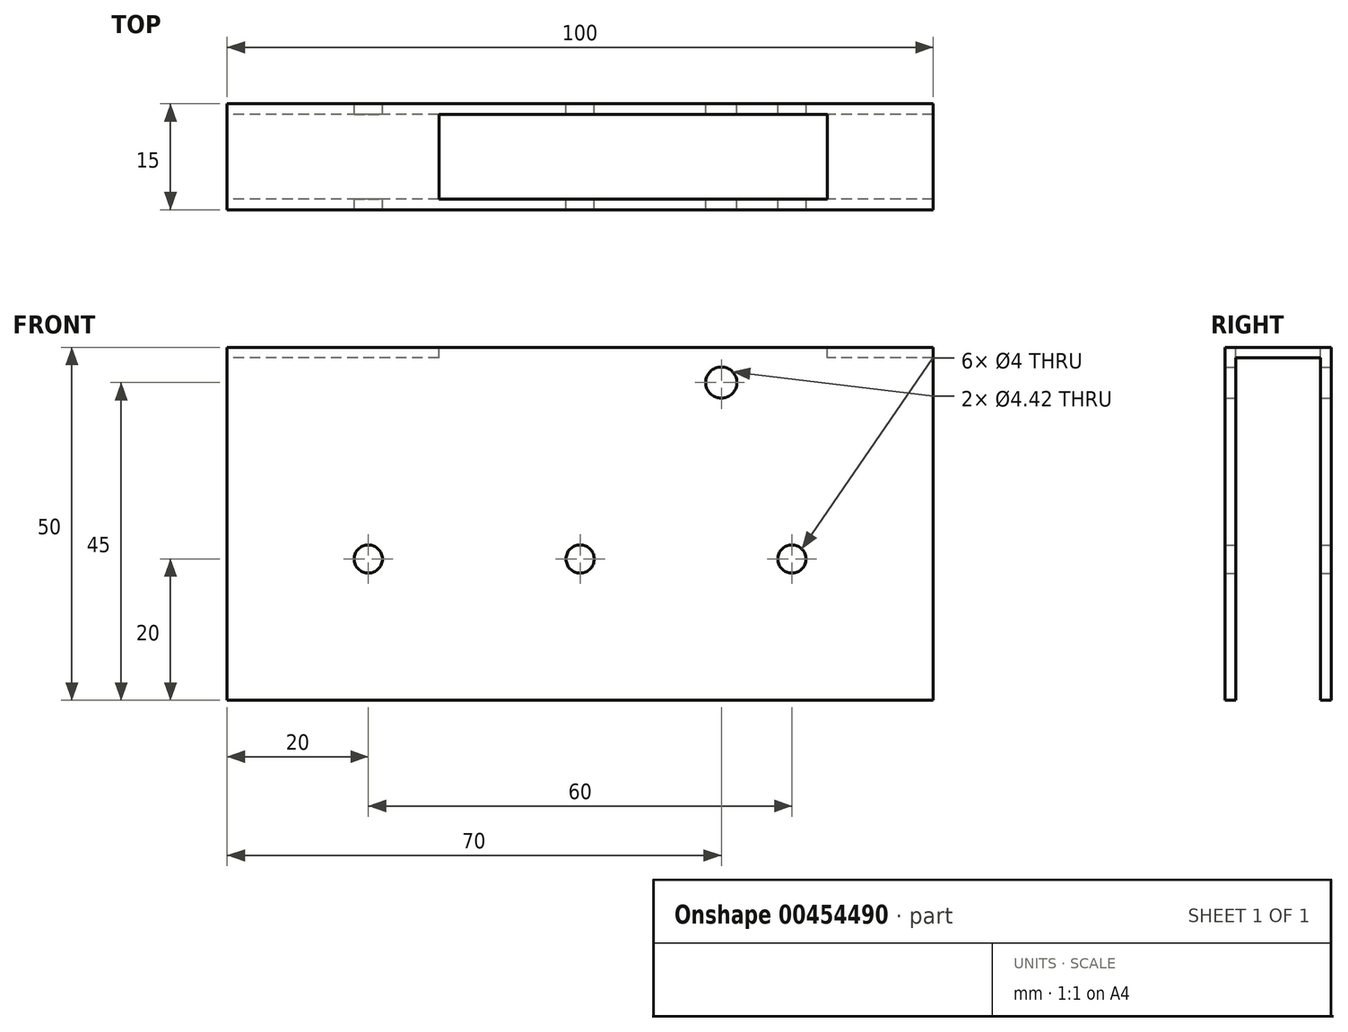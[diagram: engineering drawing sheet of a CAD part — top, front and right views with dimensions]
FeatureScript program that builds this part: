
annotation { "Feature Type Name" : "Feature", "Feature Type Description" : "" }
export const myFeature = defineFeature(function(context is Context, id is Id, definition is map)
    precondition{}
    {
        {
            var Q0;
            Q0=qCreatedBy(makeId("Front.planeOp"),FACE);
            var sketch = newSketch(context, id + "F0", { "sketchPlane" : qUnion([Q0])});
            skLineSegment(sketch, "E0.bottom", {"start": v(-50, 30) * mm, "end": v(50, 30) * mm});
            skLineSegment(sketch, "E0.top", {"start": v(-50, -20) * mm, "end": v(50, -20) * mm});
            skLineSegment(sketch, "E0.left", {"start": v(-50, 30) * mm, "end": v(-50, -20) * mm});
            skLineSegment(sketch, "E0.right", {"start": v(50, 30) * mm, "end": v(50, -20) * mm});
            skCircle(sketch, "E1", {"center": v(0, 0) * mm, "radius": 2 * mm});
            skCircle(sketch, "E2", {"center": v(-30, 0) * mm, "radius": 2 * mm});
            skCircle(sketch, "E3", {"center": v(30, 0) * mm, "radius": 2 * mm});
            skCircle(sketch, "E4", {"center": v(20, 25) * mm, "radius": 2.21 * mm});
            skSolve(sketch);
        }
        {
            var Q0;
            Q0=makeQuery(id+"F0.imprint","IMPRINT",FACE,{"disambiguationData":[TD([[makeQuery(id+"F0.imprint","IMPRINT",EDGE,{"derivedFrom":sQuery(id+"F0.wireOp",EDGE,"E0.bottom")}),-1.0]])]});
            extrude(context, id + "F1", {"entities" : qUnion([Q0]), "depth" : 15 * mm});
        }
        {
            var Q0;
            Q0=makeQuery(id+"F1.opExtrude","SWEPT_FACE",FACE,{"disambiguationData":[OSD([sQuery(id+"F0.wireOp",EDGE,"E0.left")])]});
            var sketch = newSketch(context, id + "F2", { "sketchPlane" : qUnion([Q0])});
            skLineSegment(sketch, "E5.bottom", {"start": v(1.5, -20) * mm, "end": v(13.5, -20) * mm});
            skLineSegment(sketch, "E5.top", {"start": v(1.5, 28.5) * mm, "end": v(13.5, 28.5) * mm});
            skLineSegment(sketch, "E5.left", {"start": v(1.5, -20) * mm, "end": v(1.5, 28.5) * mm});
            skLineSegment(sketch, "E5.right", {"start": v(13.5, -20) * mm, "end": v(13.5, 28.5) * mm});
            skSolve(sketch);
        }
        {
            var Q0;
            Q0 = qSketchRegion(id + "F2", true);
            extrude(context, id + "F3", {"entities" : qUnion([Q0]), "operationType" : NewBodyOperationType.REMOVE, "endBound" : BoundingType.THROUGH_ALL, "oppositeDirection" : true, "depth" : 25 * mm});
        }
        {
            var Q0;
            Q0=makeQuery(id+"F1.opExtrude","SWEPT_FACE",FACE,{"disambiguationData":[OSD([sQuery(id+"F0.wireOp",EDGE,"E0.bottom")])]});
            var sketch = newSketch(context, id + "F4", { "sketchPlane" : qUnion([Q0])});
            skLineSegment(sketch, "E6.bottom", {"start": v(35, -13.5) * mm, "end": v(-20, -13.5) * mm});
            skLineSegment(sketch, "E6.top", {"start": v(35, -1.5) * mm, "end": v(-20, -1.5) * mm});
            skLineSegment(sketch, "E6.left", {"start": v(35, -13.5) * mm, "end": v(35, -1.5) * mm});
            skLineSegment(sketch, "E6.right", {"start": v(-20, -13.5) * mm, "end": v(-20, -1.5) * mm});
            skSolve(sketch);
        }
        {
            var Q0;
            Q0 = qSketchRegion(id + "F4", true);
            extrude(context, id + "F5", {"entities" : qUnion([Q0]), "operationType" : NewBodyOperationType.REMOVE, "oppositeDirection" : true, "depth" : 25 * mm});
        }
    });
